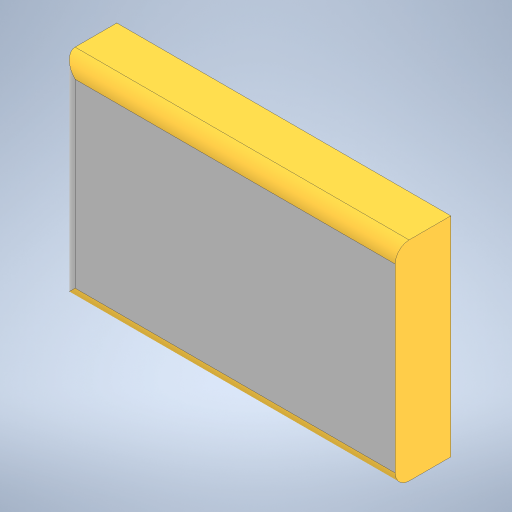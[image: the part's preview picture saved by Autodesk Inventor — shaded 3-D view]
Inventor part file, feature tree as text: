
AUTODESK INVENTOR PART (.ipt)
format: ipt  version: 2024 (Build 280153000, 153)  size: 207,872 bytes
history: native  units: in
note: dims shown in document units (in); Inventor stores cm internally (conversion verified against a paired STEP export)
features: extrude x1, fillet x1, sketch x1
ambient origin geometry x8: Origin, YZ Plane, XZ Plane, XY Plane, X Axis, Y Axis, Z Axis, Center Point
bodies: Solid1 (feature_tree)
feature tree (3):
  extrude  "Extrusion1"  Depth=1.8898in
  fillet  "Fillet1"  Radius=0.315in
  sketch  "Sketch1"  dims[d3=1.1811in d4=1.8898in d7=0.315in d8=0.0in d9=0.0787in]
